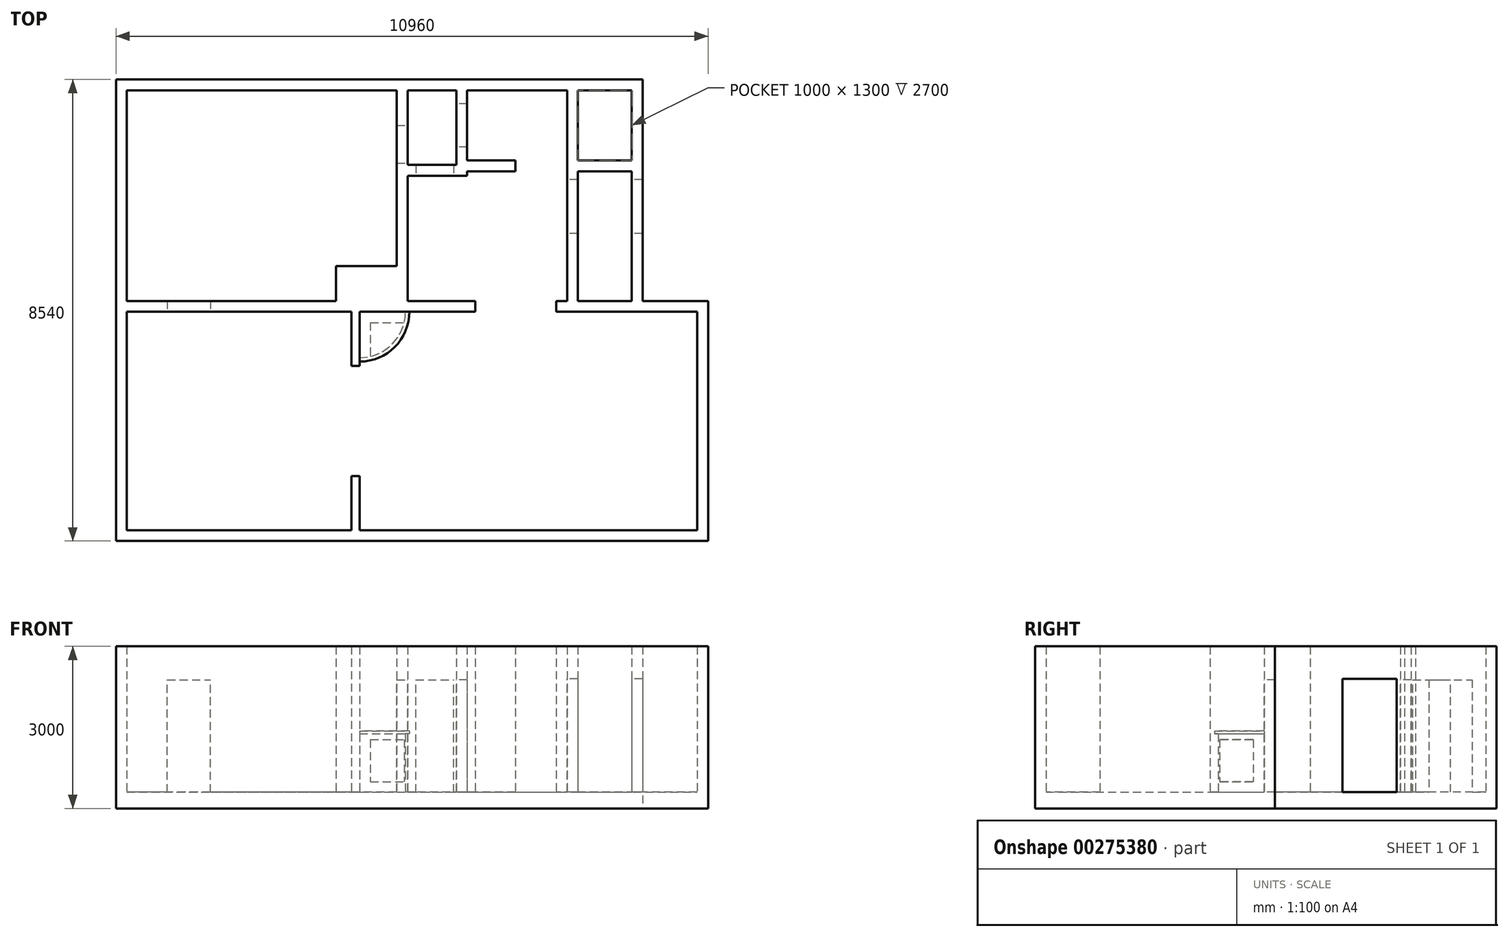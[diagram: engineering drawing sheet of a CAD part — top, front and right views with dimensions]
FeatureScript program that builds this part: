
annotation { "Feature Type Name" : "Feature", "Feature Type Description" : "" }
export const myFeature = defineFeature(function(context is Context, id is Id, definition is map)
    precondition{}
    {
        {
            var Q0;
            Q0=qCreatedBy(makeId("Top.planeOp"),FACE);
            var sketch = newSketch(context, id + "F0", { "sketchPlane" : qUnion([Q0])});
            skLineSegment(sketch, "E0.bottom", {"start": v(0, 0) * mm, "end": v(9750, 0) * mm});
            skLineSegment(sketch, "E0.top", {"start": v(0, -8540) * mm, "end": v(10960, -8540) * mm});
            skLineSegment(sketch, "E0.left", {"start": v(0, 0) * mm, "end": v(0, -8540) * mm});
            skLineSegment(sketch, "E1", {"start": v(200, -200) * mm, "end": v(200, -4100) * mm});
            skLineSegment(sketch, "E2", {"start": v(200, -4100) * mm, "end": v(4070, -4100) * mm});
            skLineSegment(sketch, "E3", {"start": v(4070, -4100) * mm, "end": v(4070, -3450) * mm});
            skLineSegment(sketch, "E4", {"start": v(4070, -3450) * mm, "end": v(5200, -3450) * mm});
            skLineSegment(sketch, "E5", {"start": v(5200, -3450) * mm, "end": v(5200, -200) * mm});
            skLineSegment(sketch, "E6", {"start": v(5200, -200) * mm, "end": v(200, -200) * mm});
            skLineSegment(sketch, "E7", {"start": v(200, -4300) * mm, "end": v(200, -8340) * mm});
            skLineSegment(sketch, "E8", {"start": v(200, -8340) * mm, "end": v(4360, -8340) * mm});
            skLineSegment(sketch, "E9", {"start": v(4360, -8340) * mm, "end": v(4360, -7340) * mm});
            skLineSegment(sketch, "E10", {"start": v(4360, -7340) * mm, "end": v(4510, -7340) * mm});
            skLineSegment(sketch, "E11", {"start": v(4510, -7340) * mm, "end": v(4510, -8340) * mm});
            skLineSegment(sketch, "E12", {"start": v(4510, -8340) * mm, "end": v(10760, -8340) * mm});
            skLineSegment(sketch, "E13", {"start": v(10760, -8340) * mm, "end": v(10760, -4300) * mm});
            skLineSegment(sketch, "E14", {"start": v(10760, -4300) * mm, "end": v(8150, -4300) * mm});
            skLineSegment(sketch, "E15", {"start": v(4510, -4300) * mm, "end": v(4510, -5300) * mm});
            skLineSegment(sketch, "E16", {"start": v(4510, -5300) * mm, "end": v(4360, -5300) * mm});
            skLineSegment(sketch, "E17", {"start": v(4360, -5300) * mm, "end": v(4360, -4300) * mm});
            skLineSegment(sketch, "E18", {"start": v(4360, -4300) * mm, "end": v(200, -4300) * mm});
            skLineSegment(sketch, "E19", {"start": v(10960, -8540) * mm, "end": v(10960, -4100) * mm});
            skLineSegment(sketch, "E20", {"start": v(10960, -4100) * mm, "end": v(9750, -4100) * mm});
            skLineSegment(sketch, "E21", {"start": v(9750, -4100) * mm, "end": v(9750, 0) * mm});
            skLineSegment(sketch, "E22.bottom", {"start": v(5400, -200) * mm, "end": v(6300, -200) * mm});
            skLineSegment(sketch, "E22.top", {"start": v(5400, -1580) * mm, "end": v(6300, -1580) * mm});
            skLineSegment(sketch, "E22.left", {"start": v(5400, -200) * mm, "end": v(5400, -1580) * mm});
            skLineSegment(sketch, "E22.right", {"start": v(6300, -200) * mm, "end": v(6300, -1580) * mm});
            skLineSegment(sketch, "E23", {"start": v(5400, -1780) * mm, "end": v(5400, -4100) * mm});
            skLineSegment(sketch, "E24", {"start": v(5400, -4100) * mm, "end": v(6650, -4100) * mm});
            skLineSegment(sketch, "E25", {"start": v(8350, -4100) * mm, "end": v(8350, -1700) * mm});
            skLineSegment(sketch, "E26", {"start": v(7393.18, -1700) * mm, "end": v(6500, -1700) * mm});
            skLineSegment(sketch, "E27", {"start": v(6500, -1700) * mm, "end": v(6500, -1780) * mm});
            skLineSegment(sketch, "E28", {"start": v(6500, -1780) * mm, "end": v(5400, -1780) * mm});
            skLineSegment(sketch, "E29", {"start": v(6650, -4100) * mm, "end": v(6650, -4300) * mm});
            skLineSegment(sketch, "E30", {"start": v(8150, -4100) * mm, "end": v(8150, -4300) * mm});
            skLineSegment(sketch, "E31.trimOffspring", {"start": v(8150, -4100) * mm, "end": v(8350, -4100) * mm});
            skLineSegment(sketch, "E32.trimOffspring", {"start": v(6650, -4300) * mm, "end": v(4510, -4300) * mm});
            skLineSegment(sketch, "E33.bottom", {"start": v(8550, -200) * mm, "end": v(9550, -200) * mm});
            skLineSegment(sketch, "E33.top", {"start": v(8550, -1500) * mm, "end": v(9550, -1500) * mm});
            skLineSegment(sketch, "E33.left", {"start": v(8550, -200) * mm, "end": v(8550, -1500) * mm});
            skLineSegment(sketch, "E33.right", {"start": v(9550, -200) * mm, "end": v(9550, -1500) * mm});
            skLineSegment(sketch, "E34.bottom", {"start": v(8550, -1700) * mm, "end": v(9550, -1700) * mm});
            skLineSegment(sketch, "E34.top", {"start": v(8550, -4100) * mm, "end": v(9550, -4100) * mm});
            skLineSegment(sketch, "E34.left", {"start": v(8550, -1700) * mm, "end": v(8550, -4100) * mm});
            skLineSegment(sketch, "E34.right", {"start": v(9550, -1700) * mm, "end": v(9550, -4100) * mm});
            skLineSegment(sketch, "E35", {"start": v(7393.18, -1700) * mm, "end": v(7393.18, -1500) * mm});
            skLineSegment(sketch, "E36", {"start": v(7393.18, -1500) * mm, "end": v(6500, -1500) * mm});
            skLineSegment(sketch, "E37", {"start": v(6500, -1500) * mm, "end": v(6500, -200) * mm});
            skLineSegment(sketch, "E38", {"start": v(6500, -200) * mm, "end": v(8350, -200) * mm});
            skLineSegment(sketch, "E39", {"start": v(8350, -200) * mm, "end": v(8350, -1700) * mm});
            skSolve(sketch);
        }
        {
            var Q0;
            Q0 = qSketchRegion(id + "F0", true);
            extrude(context, id + "F1", {"entities" : qUnion([Q0]), "depth" : 2700 * mm});
        }
        {
            var Q0;
            Q0=makeQuery(id+"F1.opExtrude","CAP_FACE",FACE,{"disambiguationData":[OSD([sQuery(id+"F0.wireOp",EDGE,"E0.bottom"),sQuery(id+"F0.wireOp",EDGE,"E0.top"),sQuery(id+"F0.wireOp",EDGE,"E0.left"),sQuery(id+"F0.wireOp",EDGE,"E0.right"),sQuery(id+"F0.wireOp",EDGE,"E1"),sQuery(id+"F0.wireOp",EDGE,"E2"),sQuery(id+"F0.wireOp",EDGE,"E3"),sQuery(id+"F0.wireOp",EDGE,"E4"),sQuery(id+"F0.wireOp",EDGE,"E5"),sQuery(id+"F0.wireOp",EDGE,"E6"),sQuery(id+"F0.wireOp",EDGE,"E7"),sQuery(id+"F0.wireOp",EDGE,"E8"),sQuery(id+"F0.wireOp",EDGE,"E9"),sQuery(id+"F0.wireOp",EDGE,"E10"),sQuery(id+"F0.wireOp",EDGE,"E11"),sQuery(id+"F0.wireOp",EDGE,"E12"),sQuery(id+"F0.wireOp",EDGE,"E13"),sQuery(id+"F0.wireOp",EDGE,"E14"),sQuery(id+"F0.wireOp",EDGE,"E15"),sQuery(id+"F0.wireOp",EDGE,"E16"),sQuery(id+"F0.wireOp",EDGE,"E17"),sQuery(id+"F0.wireOp",EDGE,"E18")])],"isStart":true});
            var sketch = newSketch(context, id + "F2", { "sketchPlane" : qUnion([Q0])});
            skLineSegment(sketch, "E40.bottom", {"start": v(0, 0) * mm, "end": v(0, 0) * mm});
            skLineSegment(sketch, "E41", {"start": v(0, 0) * mm, "end": v(9750, 0) * mm});
            skLineSegment(sketch, "E42", {"start": v(9750, 0) * mm, "end": v(9750, 4100) * mm});
            skLineSegment(sketch, "E43", {"start": v(9750, 4100) * mm, "end": v(10960, 4100) * mm});
            skLineSegment(sketch, "E44", {"start": v(10960, 4100) * mm, "end": v(10960, 8540) * mm});
            skLineSegment(sketch, "E45", {"start": v(10960, 8540) * mm, "end": v(0, 8540) * mm});
            skLineSegment(sketch, "E46", {"start": v(0, 8540) * mm, "end": v(0, 0) * mm});
            skSolve(sketch);
        }
        {
            var Q0;
            Q0 = qSketchRegion(id + "F2", true);
            extrude(context, id + "F3", {"entities" : qUnion([Q0]), "operationType" : NewBodyOperationType.ADD, "depth" : 300 * mm});
        }
        {
            var Q0;
            Q0=makeQuery(id+"F1.opExtrude","SWEPT_FACE",FACE,{"disambiguationData":[OSD([sQuery(id+"F0.wireOp",EDGE,"E28")])]});
            var sketch = newSketch(context, id + "F4", { "sketchPlane" : qUnion([Q0])});
            skLineSegment(sketch, "E47.bottom", {"start": v(5550, 0) * mm, "end": v(6250, 0) * mm});
            skLineSegment(sketch, "E47.top", {"start": v(5550, 2080) * mm, "end": v(6250, 2080) * mm});
            skLineSegment(sketch, "E47.left", {"start": v(5550, 0) * mm, "end": v(5550, 2080) * mm});
            skLineSegment(sketch, "E47.right", {"start": v(6250, 0) * mm, "end": v(6250, 2080) * mm});
            skSolve(sketch);
        }
        {
            var Q0;
            Q0 = qSketchRegion(id + "F4", true);
            var Q1;
            Q1=makeQuery(id+"F1.opExtrude","SWEPT_FACE",FACE,{"disambiguationData":[OSD([sQuery(id+"F0.wireOp",EDGE,"E22.top")])]});
            extrude(context, id + "F5", {"entities" : qUnion([Q0]), "operationType" : NewBodyOperationType.REMOVE, "endBound" : BoundingType.UP_TO_SURFACE, "oppositeDirection" : true, "endBoundEntityFace" : qUnion([Q1]), "depth" : 25 * mm});
        }
        {
            var Q0;
            Q0=makeQuery(id+"F1.opExtrude","SWEPT_FACE",FACE,{"disambiguationData":[OSD([sQuery(id+"F0.wireOp",EDGE,"E22.left")])]});
            var sketch = newSketch(context, id + "F6", { "sketchPlane" : qUnion([Q0])});
            skLineSegment(sketch, "E48.bottom", {"start": v(-1550, 0) * mm, "end": v(-850, 0) * mm});
            skLineSegment(sketch, "E48.top", {"start": v(-1550, 2080) * mm, "end": v(-850, 2080) * mm});
            skLineSegment(sketch, "E48.left", {"start": v(-1550, 0) * mm, "end": v(-1550, 2080) * mm});
            skLineSegment(sketch, "E48.right", {"start": v(-850, 0) * mm, "end": v(-850, 2080) * mm});
            skSolve(sketch);
        }
        {
            var Q0;
            Q0 = qSketchRegion(id + "F6", true);
            var Q1;
            Q1=makeQuery(id+"F1.opExtrude","SWEPT_FACE",FACE,{"disambiguationData":[OSD([sQuery(id+"F0.wireOp",EDGE,"E5")])]});
            extrude(context, id + "F7", {"entities" : qUnion([Q0]), "operationType" : NewBodyOperationType.REMOVE, "endBound" : BoundingType.UP_TO_SURFACE, "oppositeDirection" : true, "endBoundEntityFace" : qUnion([Q1]), "depth" : 25 * mm});
        }
        {
            var Q0;
            Q0=makeQuery(id+"F1.opExtrude","SWEPT_FACE",FACE,{"disambiguationData":[OSD([sQuery(id+"F0.wireOp",EDGE,"E22.right")])]});
            var sketch = newSketch(context, id + "F8", { "sketchPlane" : qUnion([Q0])});
            skLineSegment(sketch, "E49.bottom", {"start": v(450, 0) * mm, "end": v(1250, 0) * mm});
            skLineSegment(sketch, "E49.top", {"start": v(450, 2080) * mm, "end": v(1250, 2080) * mm});
            skLineSegment(sketch, "E49.left", {"start": v(450, 0) * mm, "end": v(450, 2080) * mm});
            skLineSegment(sketch, "E49.right", {"start": v(1250, 0) * mm, "end": v(1250, 2080) * mm});
            skSolve(sketch);
        }
        {
            var Q0;
            Q0 = qSketchRegion(id + "F8", true);
            var Q1;
            Q1=makeQuery(id+"F1.opExtrude","SWEPT_FACE",FACE,{"disambiguationData":[OSD([sQuery(id+"F0.wireOp",EDGE,"E37")])]});
            extrude(context, id + "F9", {"entities" : qUnion([Q0]), "operationType" : NewBodyOperationType.REMOVE, "endBound" : BoundingType.UP_TO_SURFACE, "oppositeDirection" : true, "endBoundEntityFace" : qUnion([Q1]), "depth" : 25 * mm});
        }
        {
            var Q0;
            {var subQ0=makeQuery(id+"F3.opExtrude","CAP_FACE",FACE,{"disambiguationData":[OSD([sQuery(id+"F2.wireOp",EDGE,"E41"),sQuery(id+"F2.wireOp",EDGE,"E42"),sQuery(id+"F2.wireOp",EDGE,"E43"),sQuery(id+"F2.wireOp",EDGE,"E44"),sQuery(id+"F2.wireOp",EDGE,"E45"),sQuery(id+"F2.wireOp",EDGE,"E46")])],"isStart":true});Q0=makeQuery(id+"F9.boolean.opBoolean","MERGE",FACE,{"derivedFrom":[makeQuery(id+"F7.boolean.opBoolean","MERGE",FACE,{"derivedFrom":[makeQuery(id+"F3.boolean.opBoolean","SPLIT",FACE,{"disambiguationData":[TD([makeQuery(id+"F1.opExtrude","SWEPT_FACE",FACE,{"disambiguationData":[OSD([sQuery(id+"F0.wireOp",EDGE,"E1")])]})])],"derivedFrom":subQ0}),makeQuery(id+"F5.boolean.opBoolean","MERGE",FACE,{"derivedFrom":[makeQuery(id+"F3.boolean.opBoolean","SPLIT",FACE,{"disambiguationData":[TD([makeQuery(id+"F1.opExtrude","SWEPT_FACE",FACE,{"disambiguationData":[OSD([sQuery(id+"F0.wireOp",EDGE,"E7")])]})])],"derivedFrom":subQ0}),makeQuery(id+"F3.boolean.opBoolean","SPLIT",FACE,{"disambiguationData":[TD([makeQuery(id+"F1.opExtrude","SWEPT_FACE",FACE,{"disambiguationData":[OSD([sQuery(id+"F0.wireOp",EDGE,"E22.bottom")])]})])],"derivedFrom":subQ0})],"fromTools":[makeQuery(id+"F5.opExtrude","SWEPT_FACE",FACE,{"disambiguationData":[OSD([sQuery(id+"F4.wireOp",EDGE,"E47.bottom")])]})]})],"fromTools":[makeQuery(id+"F7.opExtrude","SWEPT_FACE",FACE,{"disambiguationData":[OSD([sQuery(id+"F6.wireOp",EDGE,"E48.bottom")])]})]})],"fromTools":[makeQuery(id+"F9.opExtrude","SWEPT_FACE",FACE,{"disambiguationData":[OSD([sQuery(id+"F8.wireOp",EDGE,"E49.bottom")])]})]});}
            var sketch = newSketch(context, id + "F10", { "sketchPlane" : qUnion([Q0])});
            skLineSegment(sketch, "E50", {"start": v(4510, -4300) * mm, "end": v(4510, -5148.53) * mm});
            skLineSegment(sketch, "E51", {"start": v(4510, -5148.53) * mm, "end": v(5358.53, -4300) * mm, "construction": true});
            skLineSegment(sketch, "E52", {"start": v(5358.53, -4300) * mm, "end": v(4510, -4300) * mm});
            skArc(sketch, "E53", {"start": v(4510, -5148.53) * mm, "mid": v(5110, -4900) * mm, "end": v(5358.53, -4300) * mm});
            skSolve(sketch);
        }
        {
            var Q0;
            Q0 = qSketchRegion(id + "F10", true);
            extrude(context, id + "F11", {"entities" : qUnion([Q0]), "operationType" : NewBodyOperationType.ADD, "depth" : 1080 * mm});
        }
        {
            var Q0;
            Q0=makeQuery(id+"F11.opExtrude","CAP_FACE",FACE,{"disambiguationData":[OSD([sQuery(id+"F10.wireOp",EDGE,"E50"),sQuery(id+"F10.wireOp",EDGE,"E52"),sQuery(id+"F10.wireOp",EDGE,"E53")])],"isStart":false});
            var sketch = newSketch(context, id + "F12", { "sketchPlane" : qUnion([Q0])});
            skArc(sketch, "E54", {"start": v(4510, -5221.41) * mm, "mid": v(5161.54, -4951.54) * mm, "end": v(5431.41, -4300) * mm});
            skLineSegment(sketch, "E55", {"start": v(4510, -4300) * mm, "end": v(4510, -5221.41) * mm});
            skLineSegment(sketch, "E56", {"start": v(5431.41, -4300) * mm, "end": v(4510, -4300) * mm});
            skSolve(sketch);
        }
        {
            var Q0;
            Q0 = qSketchRegion(id + "F12", true);
            extrude(context, id + "F13", {"entities" : qUnion([Q0]), "operationType" : NewBodyOperationType.ADD, "depth" : 50 * mm});
        }
        {
            var Q0;
            Q0=makeQuery(id+"F13.opExtrude","CAP_FACE",FACE,{"disambiguationData":[OSD([sQuery(id+"F12.wireOp",EDGE,"E54"),sQuery(id+"F12.wireOp",EDGE,"E55"),sQuery(id+"F12.wireOp",EDGE,"E56")])],"isStart":false});
            var sketch = newSketch(context, id + "F14", { "sketchPlane" : qUnion([Q0])});
            skLineSegment(sketch, "E57.bottom", {"start": v(4710, -4500) * mm, "end": v(5975.34, -4500) * mm});
            skLineSegment(sketch, "E57.top", {"start": v(4710, -5490.94) * mm, "end": v(5975.34, -5490.94) * mm});
            skLineSegment(sketch, "E57.left", {"start": v(4710, -4500) * mm, "end": v(4710, -5490.94) * mm});
            skLineSegment(sketch, "E57.right", {"start": v(5975.34, -4500) * mm, "end": v(5975.34, -5490.94) * mm});
            skSolve(sketch);
        }
        {
            var Q0;
            Q0 = qSketchRegion(id + "F14", true);
            extrude(context, id + "F15", {"entities" : qUnion([Q0]), "operationType" : NewBodyOperationType.REMOVE, "oppositeDirection" : true, "depth" : 940 * mm, "hasSecondDirection" : true, "secondDirectionOppositeDirection" : true, "secondDirectionDepth" : 159 * mm});
        }
        {
            var Q0;
            Q0=makeQuery(id+"F1.opExtrude","SWEPT_FACE",FACE,{"disambiguationData":[OSD([sQuery(id+"F0.wireOp",EDGE,"E25"),sQuery(id+"F0.wireOp",EDGE,"E39")])]});
            var sketch = newSketch(context, id + "F16", { "sketchPlane" : qUnion([Q0])});
            skLineSegment(sketch, "E58.bottom", {"start": v(2850, 0) * mm, "end": v(1850, 0) * mm});
            skLineSegment(sketch, "E58.top", {"start": v(2850, 2100) * mm, "end": v(1850, 2100) * mm});
            skLineSegment(sketch, "E58.left", {"start": v(2850, 0) * mm, "end": v(2850, 2100) * mm});
            skLineSegment(sketch, "E58.right", {"start": v(1850, 0) * mm, "end": v(1850, 2100) * mm});
            skSolve(sketch);
        }
        {
            var Q0;
            Q0 = qSketchRegion(id + "F16", true);
            var Q1;
            Q1=makeQuery(id+"F3.boolean.opBoolean","MERGE",FACE,{"derivedFrom":[makeQuery(id+"F1.opExtrude","SWEPT_FACE",FACE,{"disambiguationData":[OSD([sQuery(id+"F0.wireOp",EDGE,"E21")])]}),makeQuery(id+"F3.opExtrude","SWEPT_FACE",FACE,{"disambiguationData":[OSD([sQuery(id+"F2.wireOp",EDGE,"E42")])]})]});
            extrude(context, id + "F17", {"entities" : qUnion([Q0]), "operationType" : NewBodyOperationType.REMOVE, "endBound" : BoundingType.UP_TO_SURFACE, "oppositeDirection" : true, "endBoundEntityFace" : qUnion([Q1]), "depth" : 25 * mm});
        }
        {
            var Q0;
            Q0=makeQuery(id+"F1.opExtrude","SWEPT_FACE",FACE,{"disambiguationData":[OSD([sQuery(id+"F0.wireOp",EDGE,"E18")])]});
            var sketch = newSketch(context, id + "F18", { "sketchPlane" : qUnion([Q0])});
            skLineSegment(sketch, "E59.bottom", {"start": v(950, 0) * mm, "end": v(1750, 0) * mm});
            skLineSegment(sketch, "E59.top", {"start": v(950, 2080) * mm, "end": v(1750, 2080) * mm});
            skLineSegment(sketch, "E59.left", {"start": v(950, 0) * mm, "end": v(950, 2080) * mm});
            skLineSegment(sketch, "E59.right", {"start": v(1750, 0) * mm, "end": v(1750, 2080) * mm});
            skSolve(sketch);
        }
        {
            var Q0;
            Q0 = qSketchRegion(id + "F18", true);
            var Q1;
            Q1=makeQuery(id+"F1.opExtrude","SWEPT_FACE",FACE,{"disambiguationData":[OSD([sQuery(id+"F0.wireOp",EDGE,"E2")])]});
            extrude(context, id + "F19", {"entities" : qUnion([Q0]), "operationType" : NewBodyOperationType.REMOVE, "endBound" : BoundingType.UP_TO_SURFACE, "oppositeDirection" : true, "endBoundEntityFace" : qUnion([Q1]), "depth" : 25 * mm});
        }
    });
